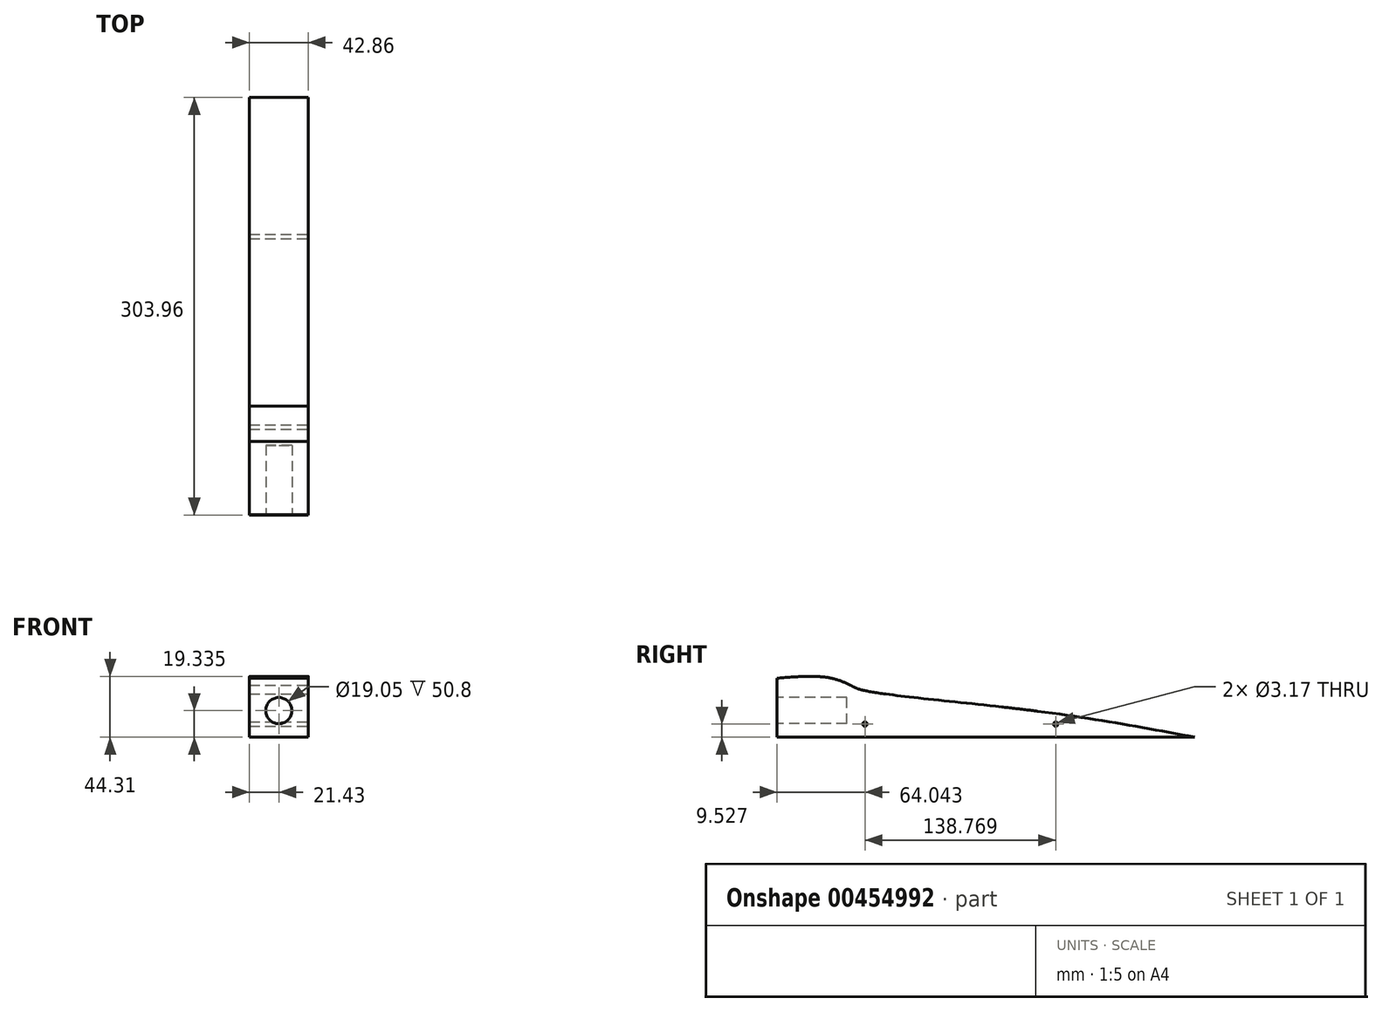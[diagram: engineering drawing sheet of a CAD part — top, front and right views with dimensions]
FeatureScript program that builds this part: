
annotation { "Feature Type Name" : "Feature", "Feature Type Description" : "" }
export const myFeature = defineFeature(function(context is Context, id is Id, definition is map)
    precondition{}
    {
        {
            var Q0;
            Q0=qCreatedBy(makeId("Right.planeOp"),FACE);
            var sketch = newSketch(context, id + "F0", { "sketchPlane" : qUnion([Q0])});
            skLineSegment(sketch, "E0", {"start": v(-152.4, 0) * mm, "end": v(152.4, 0) * mm});
            skLineSegment(sketch, "E1", {"start": v(-152.4, 0) * mm, "end": v(-152.4, 69.85) * mm});
            skLineSegment(sketch, "E2", {"start": v(152.4, 0) * mm, "end": v(152.4, 19.05) * mm});
            skLineSegment(sketch, "E3", {"start": v(152.4, 19.05) * mm, "end": v(-152.4, 69.85) * mm});
            skPoint(sketch, "E4.endSnap0", {"position": v(-152.4, 34.93) * mm});
            skLineSegment(sketch, "E5.0", {"start": v(-95.25, 50.8) * mm, "end": v(-152.4, 50.8) * mm, "construction": true});
            skLineSegment(sketch, "E5.1", {"start": v(-95.25, 50.8) * mm, "end": v(-95.25, 19.05) * mm, "construction": true});
            skLineSegment(sketch, "E5.2", {"start": v(-95.25, 19.05) * mm, "end": v(-152.4, 19.05) * mm, "construction": true});
            skSolve(sketch);
        }
        {
            var Q0;
            Q0=makeQuery(id+"F0.imprint","IMPRINT",FACE,{"disambiguationData":[TD([[makeQuery(id+"F0.imprint","IMPRINT",EDGE,{"derivedFrom":sQuery(id+"F0.wireOp",EDGE,"E0")}),1.0]])]});
            extrude(context, id + "F1", {"entities" : qUnion([Q0]), "depth" : 42.86 * mm, "symmetric" : true});
        }
        {
            var Q0;
            Q0=makeQuery(id+"F1.opExtrude","SWEPT_FACE",FACE,{"disambiguationData":[OSD([sQuery(id+"F0.wireOp",EDGE,"E1")])]});
            var sketch = newSketch(context, id + "F2", { "sketchPlane" : qUnion([Q0])});
            skLineSegment(sketch, "E6", {"start": v(21.43, 34.93) * mm, "end": v(0, 34.93) * mm, "construction": true});
            skCircle(sketch, "E7", {"center": v(0, 34.93) * mm, "radius": 9.53 * mm});
            skSolve(sketch);
        }
        {
            var Q0;
            Q0=makeQuery(id+"F2.imprint","IMPRINT",FACE,{"disambiguationData":[TD([[makeQuery(id+"F2.imprint","IMPRINT",EDGE,{"derivedFrom":sQuery(id+"F2.wireOp",EDGE,"E7")}),1.0]])]});
            var Q1;
            Q1=sQuery(id+"F2.wireOp",EDGE,"E7");
            extrude(context, id + "F3", {"entities" : qUnion([Q0]), "operationType" : NewBodyOperationType.REMOVE, "surfaceEntities" : qUnion([Q1]), "oppositeDirection" : true, "depth" : 50.8 * mm});
        }
        {
            var Q0;
            Q0=makeQuery(id+"F1.opExtrude","CAP_FACE",FACE,{"disambiguationData":[OSD([sQuery(id+"F0.wireOp",EDGE,"E0"),sQuery(id+"F0.wireOp",EDGE,"E1"),sQuery(id+"F0.wireOp",EDGE,"E2"),sQuery(id+"F0.wireOp",EDGE,"E3")])],"isStart":false});
            var sketch = newSketch(context, id + "F4", { "sketchPlane" : qUnion([Q0])});
            skLineSegment(sketch, "E8", {"start": v(-152.4, 34.93) * mm, "end": v(-152.4, 44.45) * mm, "construction": true});
            skLineSegment(sketch, "E9.0", {"start": v(-95.25, 19.05) * mm, "end": v(-152.4, 19.05) * mm, "construction": true});
            skLineSegment(sketch, "E9.1", {"start": v(-95.25, 50.8) * mm, "end": v(-95.25, 19.05) * mm, "construction": true});
            skLineSegment(sketch, "E9.2", {"start": v(-152.4, 50.8) * mm, "end": v(-95.25, 50.8) * mm, "construction": true});
            skLineSegment(sketch, "E10", {"start": v(57.15, 0) * mm, "end": v(57.15, 34.93) * mm, "construction": true});
            skLineSegment(sketch, "E11", {"start": v(-152.4, 44.45) * mm, "end": v(-101.6, 44.45) * mm, "construction": true});
            skLineSegment(sketch, "E12", {"start": v(-101.6, 44.45) * mm, "end": v(-101.6, 25.4) * mm, "construction": true});
            skLineSegment(sketch, "E13", {"start": v(-101.6, 25.4) * mm, "end": v(-152.4, 25.4) * mm, "construction": true});
            skSolve(sketch);
        }
        {
            var Q0;
            Q0=makeQuery(id+"F4.imprint","IMPRINT",FACE,{"disambiguationData":[TD([[makeQuery(id+"F4.imprint","IMPRINT",EDGE,{"derivedFrom":makeQuery(id+"F1.opExtrude","CAP_EDGE",EDGE,{"disambiguationData":[OSD([sQuery(id+"F0.wireOp",EDGE,"E0")])],"isStart":false})}),1.0]])]});
            var sketch = newSketch(context, id + "F5", { "sketchPlane" : qUnion([Q0])});
            skPoint(sketch, "E14.0.internal.orphan", {"position": v(151.58, 0) * mm});
            skPoint(sketch, "E14.2.internal.orphan", {"position": v(-35.24, 0) * mm});
            skFitSpline(sketch, "E15", {"points": [v(-94.63, 51.27) * mm, v(-114.74, 58.91) * mm, v(-152.16, 58.51) * mm], "startDerivative": vector(-42.51, 21.7) * mm, "endDerivative": vector(-71.24, -5.95) * mm});
            skFitSpline(sketch, "E16", {"points": [v(-94.63, 51.27) * mm, v(-73.06, 47) * mm, v(37.24, 34.51) * mm, v(151.56, 15.6) * mm], "startDerivative": vector(94.02, -23.14) * mm, "endDerivative": vector(262.52, -49.12) * mm});
            skFitSpline(sketch, "E17", {"points": [v(-152.16, 58.51) * mm, v(-152.4, 58.51) * mm], "startDerivative": vector(-0.24, 0) * mm, "endDerivative": vector(-0.24, 0) * mm});
            skLineSegment(sketch, "E18", {"start": v(-152.54, 15.6) * mm, "end": v(151.56, 15.6) * mm});
            skFitSpline(sketch, "E19", {"points": [v(151.56, 15.6) * mm, v(115.32, 22.37) * mm, v(37.24, 34.51) * mm, v(-73.06, 47) * mm, v(-94.63, 51.27) * mm, v(-100.74, 54.39) * mm, v(-114.74, 58.91) * mm, v(-138.66, 59.64) * mm, v(-152.16, 58.51) * mm], "startDerivative": vector(-250.82, 47.9) * mm, "endDerivative": vector(-150.48, -15.46) * mm});
            skLineSegment(sketch, "E20", {"start": v(151.56, 15.6) * mm, "end": v(-152.54, 15.6) * mm});
            skCircle(sketch, "E21", {"center": v(50.41, 25.12) * mm, "radius": 1.59 * mm});
            skPoint(sketch, "E22.center.orphan", {"position": v(-131.74, 17.18) * mm});
            skPoint(sketch, "E23.center.orphan", {"position": v(-131.88, 26.7) * mm});
            skCircle(sketch, "E24", {"center": v(-88.36, 25.12) * mm, "radius": 1.59 * mm});
            skSolve(sketch);
        }
        {
            var Q0;
            {var subQ10=sQuery(id+"F5.wireOp",EDGE,"E17");Q0=makeQuery(id+"F5.imprint","IMPRINT",FACE,{"disambiguationData":[TD([[makeQuery(id+"F5.imprint","IMPRINT",EDGE,{"derivedFrom":subQ10}),1.0]])]});}
            extrude(context, id + "F6", {"entities" : qUnion([Q0]), "operationType" : NewBodyOperationType.INTERSECT, "endBound" : BoundingType.THROUGH_ALL, "oppositeDirection" : true, "depth" : 25.4 * mm});
        }
    });
